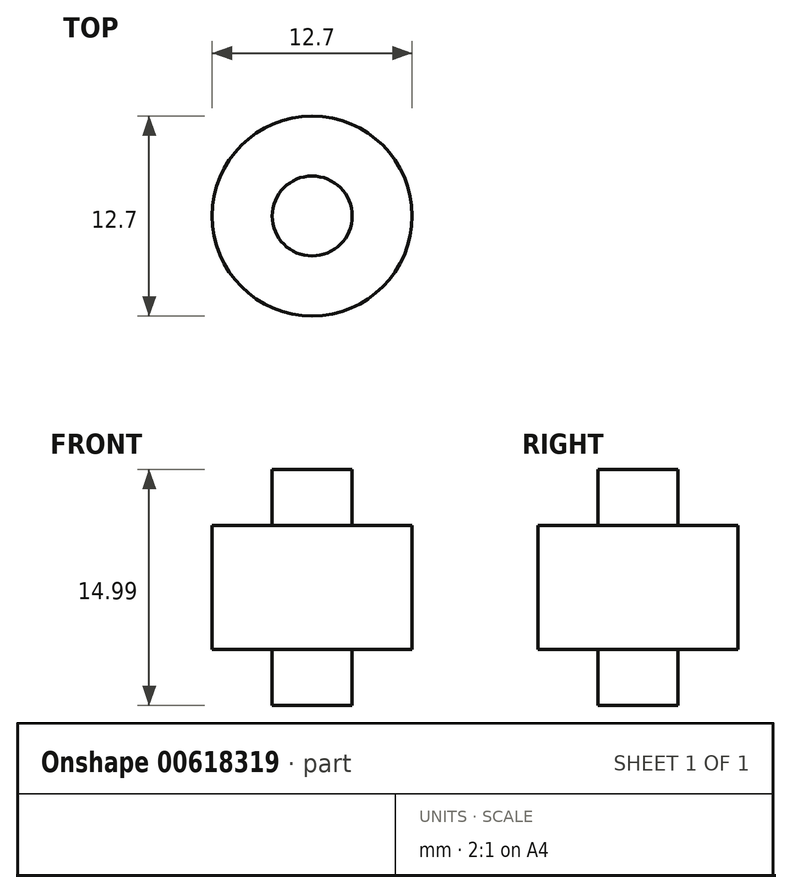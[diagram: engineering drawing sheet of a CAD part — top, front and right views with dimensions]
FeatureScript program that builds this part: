
annotation { "Feature Type Name" : "Feature", "Feature Type Description" : "" }
export const myFeature = defineFeature(function(context is Context, id is Id, definition is map)
    precondition{}
    {
        {
            var Q0;
            Q0=qCreatedBy(makeId("Top.planeOp"),FACE);
            var sketch = newSketch(context, id + "F0", { "sketchPlane" : qUnion([Q0])});
            skCircle(sketch, "E0", {"center": v(0, 0) * mm, "radius": 6.35 * mm});
            skCircle(sketch, "E1", {"center": v(0, 0) * mm, "radius": 2.54 * mm});
            skSolve(sketch);
        }
        {
            var Q0;
            Q0=makeQuery(id+"F0.imprint","IMPRINT",FACE,{"disambiguationData":[TD([[makeQuery(id+"F0.imprint","IMPRINT",EDGE,{"derivedFrom":sQuery(id+"F0.wireOp",EDGE,"E0")}),1.0]])]});
            extrude(context, id + "F1", {"entities" : qUnion([Q0]), "depth" : 7.87 * mm, "offsetDistance" : 25.4 * mm});
        }
        {
            var Q0;
            Q0=qCreatedBy(makeId("Top.planeOp"),FACE);
            var sketch = newSketch(context, id + "F2", { "sketchPlane" : qUnion([Q0])});
            skCircle(sketch, "E2", {"center": v(0, 0) * mm, "radius": 2.54 * mm});
            skSolve(sketch);
        }
        {
            var Q0;
            Q0=makeQuery(id+"F2.imprint","IMPRINT",FACE,{"disambiguationData":[TD([[makeQuery(id+"F2.imprint","IMPRINT",EDGE,{"derivedFrom":sQuery(id+"F2.wireOp",EDGE,"E2")}),1.0]])]});
            extrude(context, id + "F3", {"entities" : qUnion([Q0]), "operationType" : NewBodyOperationType.ADD, "depth" : 11.43 * mm, "offsetDistance" : 25.4 * mm});
        }
        {
            var Q0;
            Q0=qCreatedBy(makeId("Top.planeOp"),FACE);
            var sketch = newSketch(context, id + "F4", { "sketchPlane" : qUnion([Q0])});
            skCircle(sketch, "E3", {"center": v(0, 0) * mm, "radius": 2.54 * mm});
            skSolve(sketch);
        }
        {
            var Q0;
            Q0=makeQuery(id+"F4.imprint","IMPRINT",FACE,{"disambiguationData":[TD([[makeQuery(id+"F4.imprint","IMPRINT",EDGE,{"derivedFrom":sQuery(id+"F4.wireOp",EDGE,"E3")}),1.0]])]});
            extrude(context, id + "F5", {"entities" : qUnion([Q0]), "operationType" : NewBodyOperationType.ADD, "oppositeDirection" : true, "depth" : 3.56 * mm, "offsetDistance" : 25.4 * mm});
        }
    });
